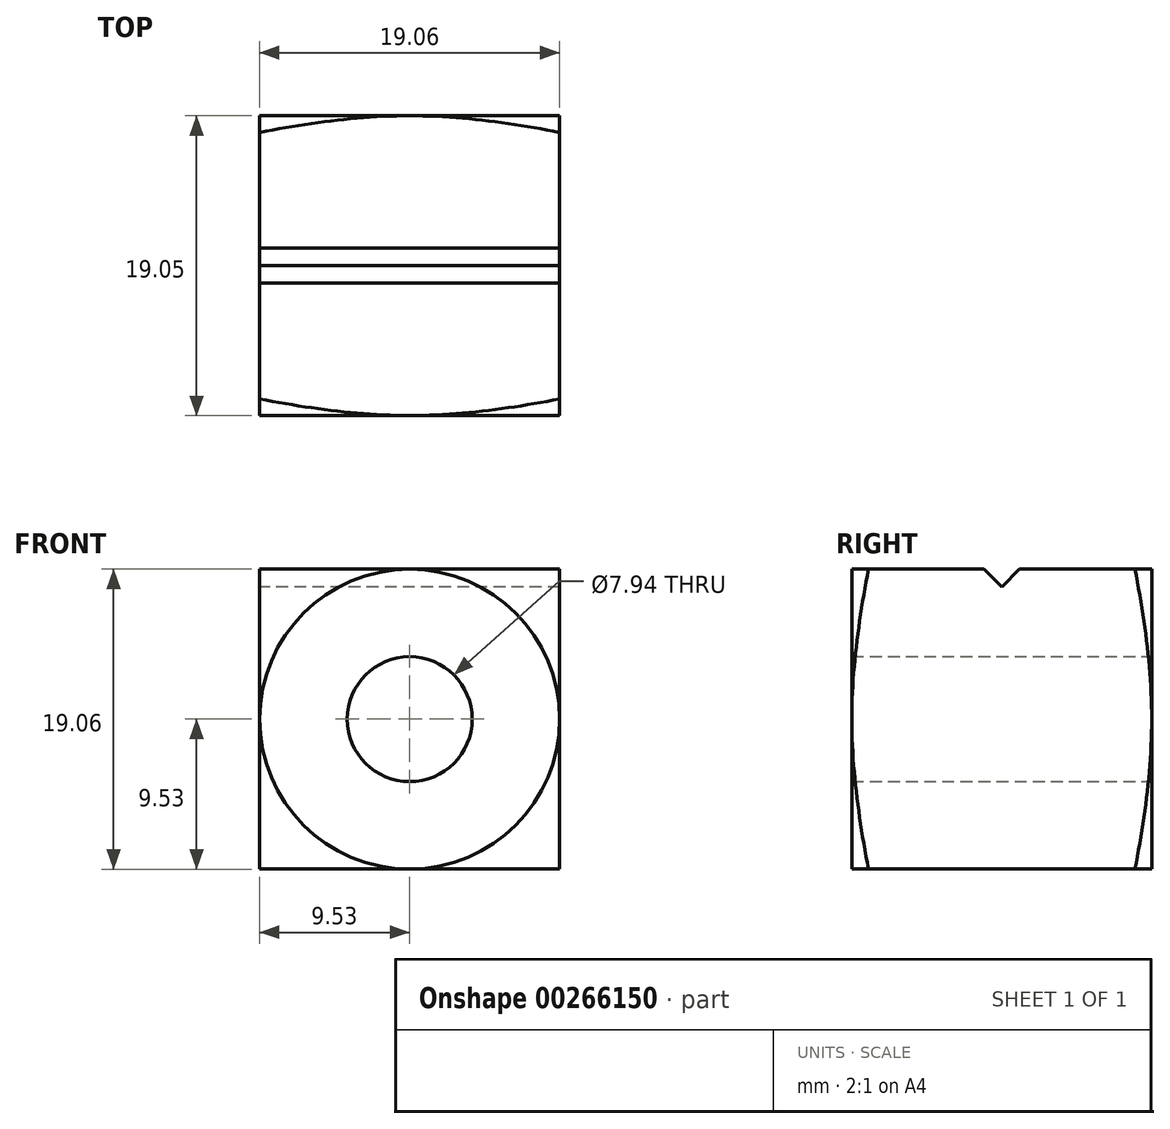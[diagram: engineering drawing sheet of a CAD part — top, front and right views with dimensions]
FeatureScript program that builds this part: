
annotation { "Feature Type Name" : "Feature", "Feature Type Description" : "" }
export const myFeature = defineFeature(function(context is Context, id is Id, definition is map)
    precondition{}
    {
        {
            var Q0;
            Q0=qCreatedBy(makeId("Front.planeOp"),FACE);
            var sketch = newSketch(context, id + "F0", { "sketchPlane" : qUnion([Q0])});
            skLineSegment(sketch, "E0.bottom", {"start": v(9.53, 9.53) * mm, "end": v(-9.52, 9.53) * mm});
            skLineSegment(sketch, "E0.top", {"start": v(9.52, -9.52) * mm, "end": v(-9.53, -9.52) * mm});
            skLineSegment(sketch, "E0.left", {"start": v(9.53, 9.53) * mm, "end": v(9.53, -9.52) * mm});
            skLineSegment(sketch, "E0.right", {"start": v(-9.52, 9.53) * mm, "end": v(-9.53, -9.52) * mm});
            skPoint(sketch, "E0.middle", {"position": v(0, 0) * mm});
            skSolve(sketch);
        }
        {
            var Q0;
            Q0=makeQuery(id+"F0.imprint","IMPRINT",FACE,{"disambiguationData":[TD([[makeQuery(id+"F0.imprint","IMPRINT",EDGE,{"derivedFrom":sQuery(id+"F0.wireOp",EDGE,"E0.bottom")}),1.0]])]});
            extrude(context, id + "F1", {"entities" : qUnion([Q0]), "depth" : 9.52 * mm});
        }
        {
            var Q0;
            Q0=makeQuery(id+"F1.opExtrude","CAP_FACE",FACE,{"disambiguationData":[OSD([sQuery(id+"F0.wireOp",EDGE,"E0.bottom"),sQuery(id+"F0.wireOp",EDGE,"E0.top"),sQuery(id+"F0.wireOp",EDGE,"E0.left"),sQuery(id+"F0.wireOp",EDGE,"E0.right")])],"isStart":true});
            var sketch = newSketch(context, id + "F2", { "sketchPlane" : qUnion([Q0])});
            skCircle(sketch, "E1", {"center": v(0, 0) * mm, "radius": 9.53 * mm});
            skSolve(sketch);
        }
        {
            var Q0;
            Q0=qCreatedBy(makeId("Right.planeOp"),FACE);
            var sketch = newSketch(context, id + "F3", { "sketchPlane" : qUnion([Q0])});
            skLineSegment(sketch, "E2", {"start": v(0, 0) * mm, "end": v(0, 9.53) * mm});
            skLineSegment(sketch, "E3", {"start": v(0, 9.53) * mm, "end": v(0, 20.34) * mm});
            skLineSegment(sketch, "E4", {"start": v(0, 20.34) * mm, "end": v(-2.9, 20.34) * mm});
            skLineSegment(sketch, "E5", {"start": v(-2.9, 20.34) * mm, "end": v(0, 9.53) * mm});
            skSolve(sketch);
        }
        {
            var Q0;
            Q0=makeQuery(id+"F3.imprint","IMPRINT",FACE,{"disambiguationData":[TD([[makeQuery(id+"F3.imprint","IMPRINT",EDGE,{"derivedFrom":sQuery(id+"F3.wireOp",EDGE,"E3")}),1.0]])]});
            var Q1;
            Q1=sQuery(id+"F2.wireOp",EDGE,"E1");
            revolve(context, id + "F4", {"operationType" : NewBodyOperationType.REMOVE, "entities" : qUnion([Q0]), "axis" : qUnion([Q1]), "revolveType" : RevolveType.FULL, "oppositeDirection" : true});
        }
        {
            var Q0;
            Q0=makeQuery(id+"F1.opExtrude","CAP_FACE",FACE,{"disambiguationData":[OSD([sQuery(id+"F0.wireOp",EDGE,"E0.bottom"),sQuery(id+"F0.wireOp",EDGE,"E0.top"),sQuery(id+"F0.wireOp",EDGE,"E0.left"),sQuery(id+"F0.wireOp",EDGE,"E0.right")])],"isStart":true});
            var sketch = newSketch(context, id + "F5", { "sketchPlane" : qUnion([Q0])});
            skCircle(sketch, "E6", {"center": v(0, 0) * mm, "radius": 3.97 * mm});
            skSolve(sketch);
        }
        {
            var Q0;
            Q0=makeQuery(id+"F5.imprint","IMPRINT",FACE,{"disambiguationData":[TD([[makeQuery(id+"F5.imprint","IMPRINT",EDGE,{"derivedFrom":sQuery(id+"F5.wireOp",EDGE,"E6")}),1.0]])]});
            extrude(context, id + "F6", {"entities" : qUnion([Q0]), "operationType" : NewBodyOperationType.REMOVE, "oppositeDirection" : true, "depth" : 9.52 * mm});
        }
        {
            var Q0;
            Q0=makeQuery(id+"F1.opExtrude","SWEPT_BODY",BODY,{"disambiguationData":[OSD([sQuery(id+"F0.wireOp",EDGE,"E0.bottom"),sQuery(id+"F0.wireOp",EDGE,"E0.top"),sQuery(id+"F0.wireOp",EDGE,"E0.left"),sQuery(id+"F0.wireOp",EDGE,"E0.right")])]});
            var Q1;
            Q1=makeQuery(id+"F1.opExtrude","CAP_FACE",FACE,{"disambiguationData":[OSD([sQuery(id+"F0.wireOp",EDGE,"E0.bottom"),sQuery(id+"F0.wireOp",EDGE,"E0.top"),sQuery(id+"F0.wireOp",EDGE,"E0.left"),sQuery(id+"F0.wireOp",EDGE,"E0.right")])],"isStart":false});
            mirror(context, id + "F7", {"operationType" : NewBodyOperationType.ADD, "entities" : qUnion([Q0]), "mirrorPlane" : qUnion([Q1])});
        }
        {
            var Q0;
            {var subQ0=makeQuery(id+"F1.opExtrude","SWEPT_FACE",FACE,{"disambiguationData":[OSD([sQuery(id+"F0.wireOp",EDGE,"E0.right")])]});Q0=makeQuery(id+"F7.boolean.opBoolean","MERGE",FACE,{"derivedFrom":[subQ0,makeQuery(id+"F7.opPattern","COPY",FACE,{"derivedFrom":subQ0,"instanceName":"1"})]});}
            var sketch = newSketch(context, id + "F8", { "sketchPlane" : qUnion([Q0])});
            skPoint(sketch, "E7.endSnap0", {"position": v(9.53, 9.53) * mm});
            skLineSegment(sketch, "E8", {"start": v(9.53, 8.4) * mm, "end": v(8.4, 9.53) * mm});
            skLineSegment(sketch, "E9", {"start": v(9.53, 8.4) * mm, "end": v(10.64, 9.53) * mm});
            skSolve(sketch);
        }
        {
            var Q0;
            {var subQ0=sQuery(id+"F8.wireOp",EDGE,"E8");Q0=makeQuery(id+"F8.imprint","IMPRINT",FACE,{"disambiguationData":[TD([[makeQuery(id+"F8.imprint","IMPRINT",EDGE,{"derivedFrom":subQ0}),-1.0]])]});}
            extrude(context, id + "F9", {"entities" : qUnion([Q0]), "operationType" : NewBodyOperationType.REMOVE, "oppositeDirection" : true, "depth" : 19.05 * mm});
        }
    });
